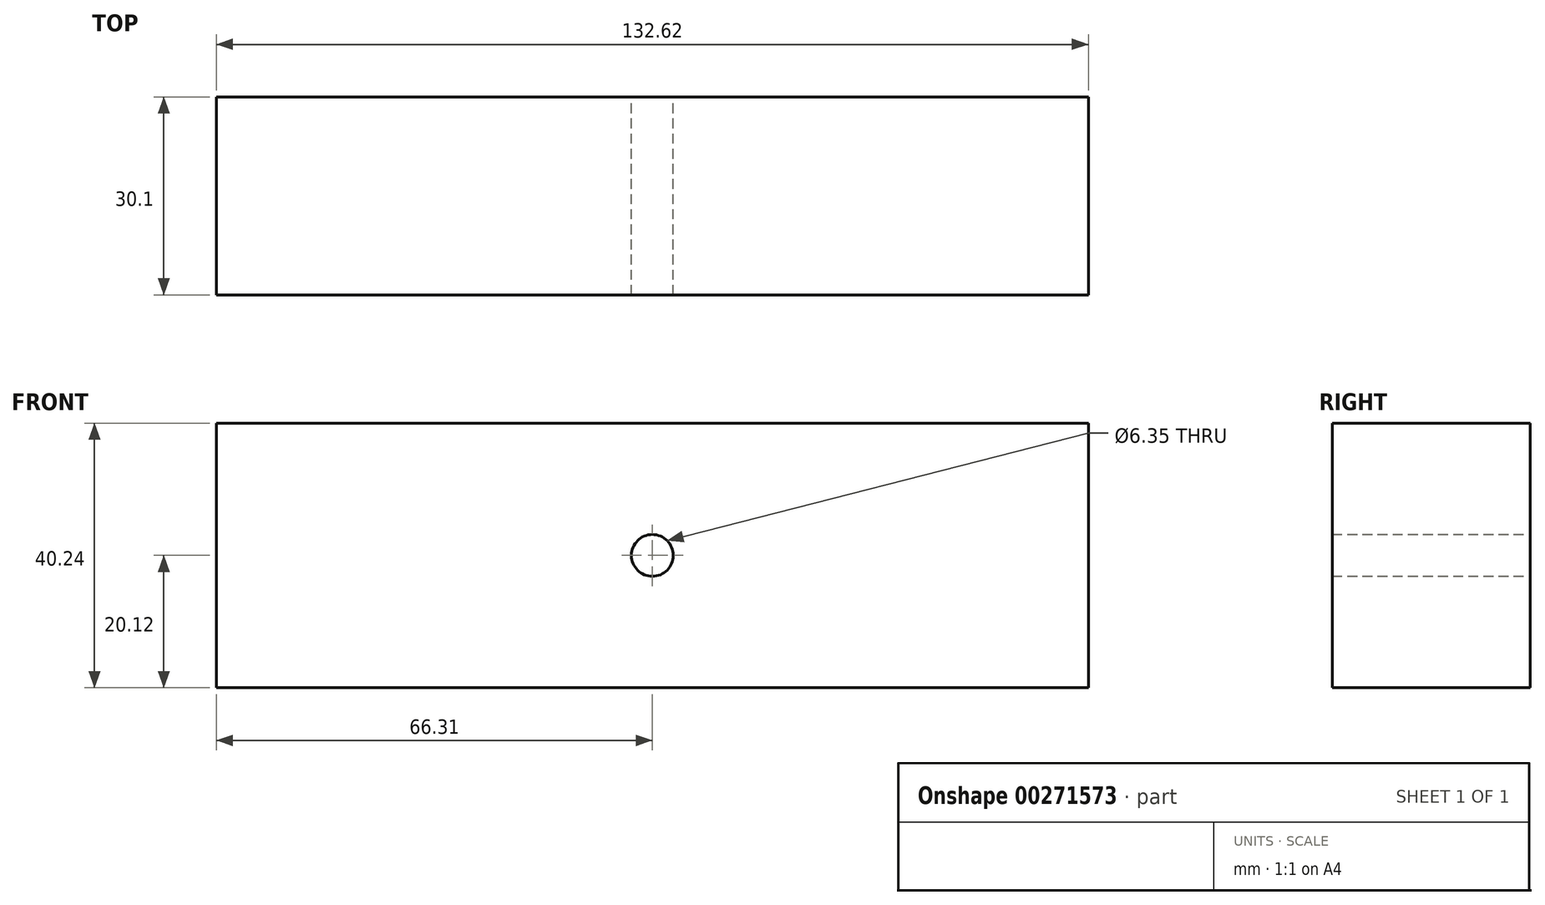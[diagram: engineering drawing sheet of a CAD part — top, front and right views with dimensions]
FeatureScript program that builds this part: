
annotation { "Feature Type Name" : "Feature", "Feature Type Description" : "" }
export const myFeature = defineFeature(function(context is Context, id is Id, definition is map)
    precondition{}
    {
        {
            var Q0;
            Q0=qCreatedBy(makeId("Front.planeOp"),FACE);
            var sketch = newSketch(context, id + "F0", { "sketchPlane" : qUnion([Q0])});
            skLineSegment(sketch, "E0.bottom", {"start": v(66.31, 20.12) * mm, "end": v(-66.31, 20.12) * mm});
            skLineSegment(sketch, "E0.top", {"start": v(66.31, -20.12) * mm, "end": v(-66.31, -20.12) * mm});
            skLineSegment(sketch, "E0.left", {"start": v(66.31, 20.12) * mm, "end": v(66.31, -20.12) * mm});
            skLineSegment(sketch, "E0.right", {"start": v(-66.31, 20.12) * mm, "end": v(-66.31, -20.12) * mm});
            skPoint(sketch, "E0.middle", {"position": v(0, 0) * mm});
            skSolve(sketch);
        }
        {
            var Q0;
            Q0=makeQuery(id+"F0.imprint","IMPRINT",FACE,{"disambiguationData":[TD([[makeQuery(id+"F0.imprint","IMPRINT",EDGE,{"derivedFrom":sQuery(id+"F0.wireOp",EDGE,"E0.bottom")}),1.0]])]});
            extrude(context, id + "F1", {"entities" : qUnion([Q0]), "depth" : 30.1 * mm});
        }
        {
            var Q0;
            Q0=sQuery(id+"F0.wireOp",VERTEX,"E0.middle");
            var Q1;
            Q1=makeQuery(id+"F1.opExtrude","SWEPT_BODY",BODY,{"disambiguationData":[OSD([sQuery(id+"F0.wireOp",EDGE,"E0.bottom"),sQuery(id+"F0.wireOp",EDGE,"E0.top"),sQuery(id+"F0.wireOp",EDGE,"E0.left"),sQuery(id+"F0.wireOp",EDGE,"E0.right")])]});
            hole(context, id + "F2", {"style" : HoleStyle.SIMPLE, "endStyle" : HoleEndStyle.THROUGH, "oppositeDirection" : true, "holeDiameter" : 6.35 * mm, "tappedDepth" : 12.7 * mm, "tapClearance" : 3, "locations" : qUnion([Q0]), "scope" : qUnion([Q1])});
        }
    });
